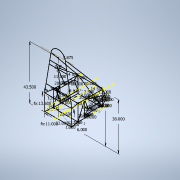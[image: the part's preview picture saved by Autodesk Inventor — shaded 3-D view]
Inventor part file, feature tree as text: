
AUTODESK INVENTOR PART (.ipt)
format: ipt  version: 2021 (Build 250183000, 183)  size: 211,456 bytes
history: native  units: in
note: dims shown in document units (in); Inventor stores cm internally (conversion verified against a paired STEP export)
features: sketch x17, plane x17, other x1
ambient origin geometry x8: Origin, YZ Plane, XZ Plane, XY Plane, X Axis, Y Axis, Z Axis, Center Point
feature tree (35):
  sketch  "Sketch1"  dims[d0=22.0in d3=20.0in d4=35.0in d5=38.0in d6=13.5in d7=13.5in d8=13.0in d9=22.0in]
  plane  "Work Plane2"
  sketch  "Sketch5"  dims[d11=10.0in]
  plane  "Work Plane1"
  sketch  "Sketch3"  dims[d10=11.0in]
  plane  "Work Plane3"
  sketch  "Sketch6"  dims[d12=20.0in]
  plane  "Work Plane4"
  sketch  "Sketch7"  dims[d16=14.625in]
  plane  "Work Plane5"
  sketch  "Sketch8"  dims[d17=2.0in]
  plane  "Work Plane7"
  sketch  "Sketch9"  dims[d18=-6.5in]
  plane  "Work Plane8"
  sketch  "Sketch10"  dims[d19=6.0in]
  plane  "Work Plane9"
  sketch  "Sketch11"  dims[d20=1.0in]
  plane  "Work Plane10"
  sketch  "Sketch13"  dims[d21=20.0in]
  plane  "Work Plane11"
  sketch  "Sketch14"  dims[d22=13.0in d25=-26.0in]
  plane  "Work Plane12"
  sketch  "Sketch15"  dims[d26=20.0in]
  plane  "Work Plane13"
  sketch  "Sketch16"  dims[d30=20.0in]
  plane  "Work Plane15"
  sketch  "Sketch17"  dims[d31=13.0in]
  plane  "Work Plane16"
  sketch  "Sketch18"  dims[d32=14.625in]
  plane  "Work Plane17"
  sketch  "Sketch19"  dims[d34=13.5in]
  plane  "Work Plane18"
  sketch  "Sketch20"  dims[d35=13.5in d36=-10.0in d37=20.0in d38=14.625in d39=2.0in d40=20.0in d41=13.0in d42=13.0in d43=14.625in d47=8.0in d48=3.0in d49=3.0in d50=2.0in d51=2.0in d52=1.25in d53=1.25in d54=15.625in d55=0.5in d56=2.0in d58=2.0in d59=1.25in d60=2.0in d61=1.25in d62=0.8532in d63=11.5in d65=0.5in d66=-0.8532in d67=11.5in d68=7.3125in d69=0.5in d70=20.5in d75=3.0in d76=3.0in d78=5.0in d79=8.0in d80=1.5in d81=7.8125in d82=20.5in d83=0.75in d84=0.75in d85=0.75in d86=21.5in d88=0.75in d89=20.0in d90=7.5in d93=5.875in d94=43.5in]
  other  "Work Axis1"
  plane  "Work Plane14"
